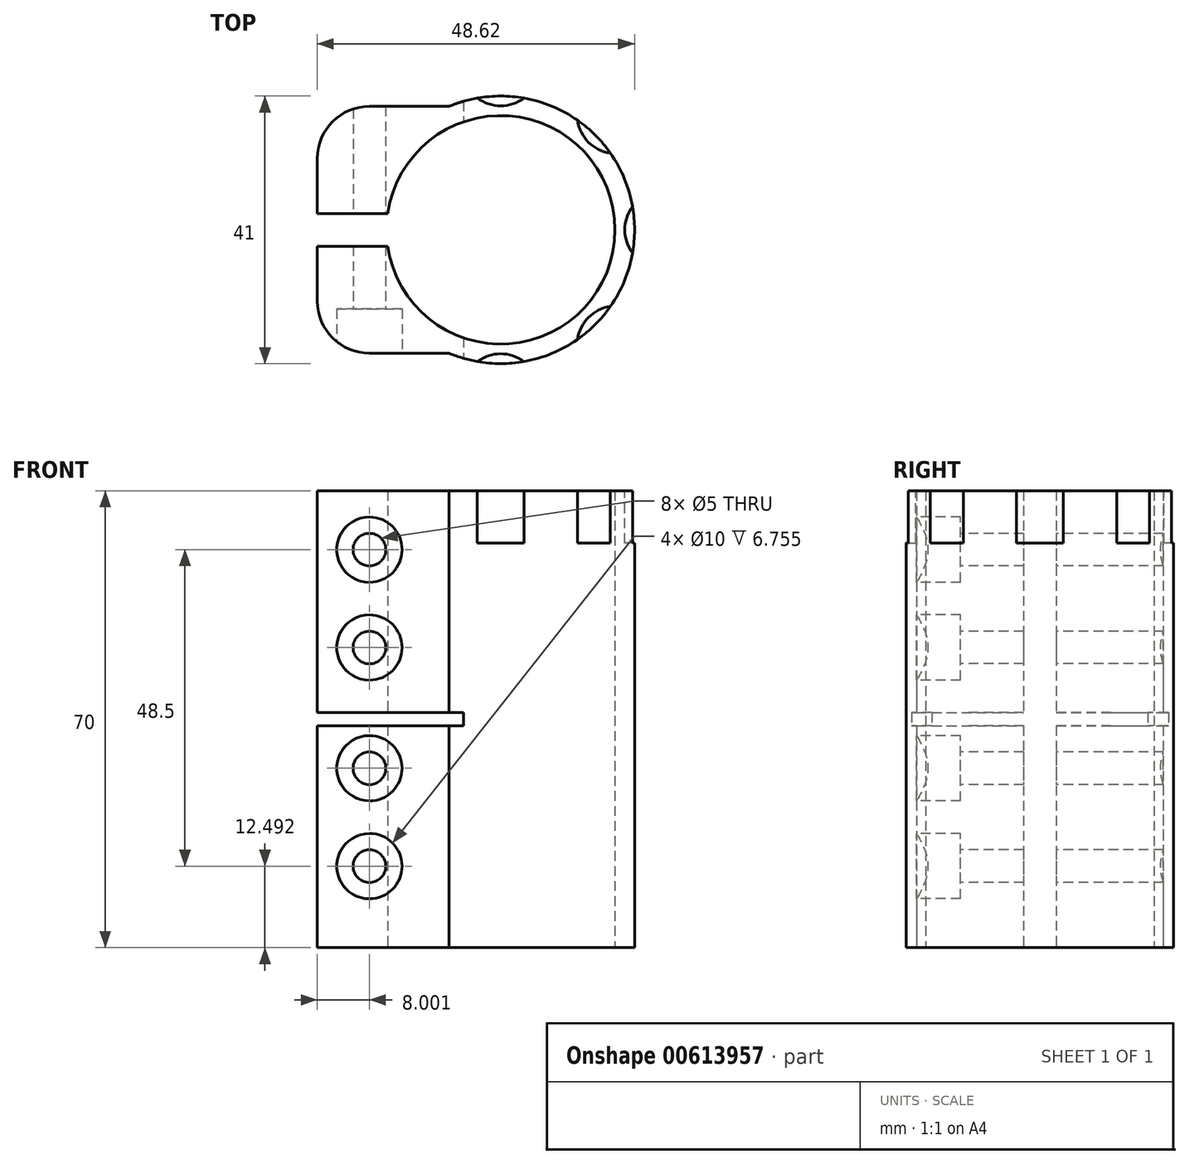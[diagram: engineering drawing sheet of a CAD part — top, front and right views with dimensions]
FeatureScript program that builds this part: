
annotation { "Feature Type Name" : "Feature", "Feature Type Description" : "" }
export const myFeature = defineFeature(function(context is Context, id is Id, definition is map)
    precondition{}
    {
        {
            var Q0;
            Q0=qCreatedBy(makeId("Top.planeOp"),FACE);
            var sketch = newSketch(context, id + "F0", { "sketchPlane" : qUnion([Q0])});
            skArc(sketch, "E0", {"start": v(-17.32, -2.5) * mm, "mid": v(17.5, 0) * mm, "end": v(-17.32, 2.5) * mm});
            skLineSegment(sketch, "E1", {"start": v(-7.92, 18.9) * mm, "end": v(-20.12, 18.9) * mm});
            skLineSegment(sketch, "E2", {"start": v(-28.12, 10.9) * mm, "end": v(-28.12, 2.5) * mm});
            skLineSegment(sketch, "E3", {"start": v(-28.12, 2.5) * mm, "end": v(-17.32, 2.5) * mm});
            skPoint(sketch, "E4.visualSharp", {"position": v(-28.12, 18.9) * mm});
            skArc(sketch, "E4.filletArc", {"start": v(-20.12, 18.9) * mm, "mid": v(-25.78, 16.57) * mm, "end": v(-28.12, 10.9) * mm});
            skLineSegment(sketch, "E5", {"start": v(0, 0) * mm, "end": v(40.9, 0) * mm, "construction": true});
            skArc(sketch, "E6.MirrorCS", {"start": v(-20.12, -18.9) * mm, "mid": v(-25.78, -16.57) * mm, "end": v(-28.12, -10.9) * mm});
            skLineSegment(sketch, "E7.MirrorCS", {"start": v(-7.92, -18.9) * mm, "end": v(-20.12, -18.9) * mm});
            skLineSegment(sketch, "E8.MirrorCS", {"start": v(-28.12, -2.5) * mm, "end": v(-17.32, -2.5) * mm});
            skLineSegment(sketch, "E9.MirrorCS", {"start": v(-28.12, -10.9) * mm, "end": v(-28.12, -2.5) * mm});
            skArc(sketch, "E10.trimOffspring", {"start": v(-7.92, -18.9) * mm, "mid": v(20.5, 0) * mm, "end": v(-7.92, 18.9) * mm});
            skSolve(sketch);
        }
        {
            var Q0;
            Q0 = qSketchRegion(id + "F0", true);
            extrude(context, id + "F1", {"entities" : qUnion([Q0]), "endBound" : BoundingType.SYMMETRIC, "depth" : 70 * mm, "offsetDistance" : 25 * mm});
        }
        {
            var Q0;
            Q0=makeQuery(id+"F1.opExtrude","SWEPT_FACE",FACE,{"disambiguationData":[OSD([sQuery(id+"F0.wireOp",EDGE,"E7.MirrorCS")])]});
            var sketch = newSketch(context, id + "F2", { "sketchPlane" : qUnion([Q0])});
            skPoint(sketch, "E11", {"position": v(-20.12, 26) * mm});
            skPoint(sketch, "E12", {"position": v(-20.12, 11) * mm});
            skPoint(sketch, "E13", {"position": v(-20.12, -7.5) * mm});
            skPoint(sketch, "E14", {"position": v(-20.12, -22.5) * mm});
            skPoint(sketch, "E15", {"position": v(0, 1.74) * mm});
            skSolve(sketch);
        }
        {
            var Q0;
            Q0=sQuery(id+"F2.wireOp",VERTEX,"E14");
            var Q1;
            Q1=sQuery(id+"F2.wireOp",VERTEX,"E13");
            var Q2;
            Q2=sQuery(id+"F2.wireOp",VERTEX,"E11");
            var Q3;
            Q3=sQuery(id+"F2.wireOp",VERTEX,"E12");
            var Q4;
            Q4=makeQuery(id+"F1.opExtrude","SWEPT_BODY",BODY,{"disambiguationData":[OSD([sQuery(id+"F0.wireOp",EDGE,"E0"),sQuery(id+"F0.wireOp",EDGE,"E1"),sQuery(id+"F0.wireOp",EDGE,"E2"),sQuery(id+"F0.wireOp",EDGE,"E3"),sQuery(id+"F0.wireOp",EDGE,"E4.filletArc"),sQuery(id+"F0.wireOp",EDGE,"E6.MirrorCS"),sQuery(id+"F0.wireOp",EDGE,"E7.MirrorCS"),sQuery(id+"F0.wireOp",EDGE,"E8.MirrorCS"),sQuery(id+"F0.wireOp",EDGE,"E9.MirrorCS"),sQuery(id+"F0.wireOp",EDGE,"E10.trimOffspring")])]});
            hole(context, id + "F3", {"style" : HoleStyle.C_BORE, "endStyle" : HoleEndStyle.THROUGH, "holeDiameter" : 5 * mm, "cBoreDiameter" : 10 * mm, "cBoreDepth" : 5 * mm, "majorDiameter" : 5 * mm, "isTappedThrough" : true, "tappedDepth" : 12 * mm, "tapClearance" : 3, "locations" : qUnion([Q0, Q1, Q2, Q3]), "scope" : qUnion([Q4])});
        }
        {
            var Q0;
            Q0=qCreatedBy(makeId("Front.planeOp"),FACE);
            var sketch = newSketch(context, id + "F4", { "sketchPlane" : qUnion([Q0])});
            skLineSegment(sketch, "E16.bottom", {"start": v(-28.12, 1) * mm, "end": v(-5.72, 1) * mm});
            skLineSegment(sketch, "E16.top", {"start": v(-28.12, -1) * mm, "end": v(-5.72, -1) * mm});
            skLineSegment(sketch, "E16.left", {"start": v(-28.12, 1) * mm, "end": v(-28.12, -1) * mm});
            skLineSegment(sketch, "E16.right", {"start": v(-5.72, 1) * mm, "end": v(-5.72, -1) * mm});
            skSolve(sketch);
        }
        {
            var Q0;
            Q0 = qSketchRegion(id + "F4", true);
            extrude(context, id + "F5", {"entities" : qUnion([Q0]), "operationType" : NewBodyOperationType.REMOVE, "endBound" : BoundingType.SYMMETRIC, "oppositeDirection" : true, "depth" : 50 * mm, "offsetDistance" : 25 * mm});
        }
        {
            var Q0;
            Q0=makeQuery(id+"F1.opExtrude","CAP_FACE",FACE,{"disambiguationData":[OSD([sQuery(id+"F0.wireOp",EDGE,"E0"),sQuery(id+"F0.wireOp",EDGE,"E1"),sQuery(id+"F0.wireOp",EDGE,"E2"),sQuery(id+"F0.wireOp",EDGE,"E3"),sQuery(id+"F0.wireOp",EDGE,"E4.filletArc"),sQuery(id+"F0.wireOp",EDGE,"E6.MirrorCS"),sQuery(id+"F0.wireOp",EDGE,"E7.MirrorCS"),sQuery(id+"F0.wireOp",EDGE,"E8.MirrorCS"),sQuery(id+"F0.wireOp",EDGE,"E9.MirrorCS"),sQuery(id+"F0.wireOp",EDGE,"E10.trimOffspring")])],"isStart":false});
            var sketch = newSketch(context, id + "F6", { "sketchPlane" : qUnion([Q0])});
            skCircle(sketch, "E17", {"center": v(0, -25) * mm, "radius": 6 * mm});
            skCircle(sketch, "E18.1.0", {"center": v(17.68, -17.68) * mm, "radius": 6 * mm});
            skCircle(sketch, "E18.2.0", {"center": v(25, 0) * mm, "radius": 6 * mm});
            skCircle(sketch, "E18.3.0", {"center": v(17.68, 17.68) * mm, "radius": 6 * mm});
            skCircle(sketch, "E18.4.0", {"center": v(0, 25) * mm, "radius": 6 * mm});
            skPoint(sketch, "E18.center", {"position": v(0, 0) * mm});
            skLineSegment(sketch, "E18.anchor1", {"start": v(0, 0) * mm, "end": v(0, -25) * mm, "construction": true});
            skLineSegment(sketch, "E18.anchor2", {"start": v(0, 0) * mm, "end": v(0, 25) * mm, "construction": true});
            skSolve(sketch);
        }
        {
            var Q0;
            Q0 = qSketchRegion(id + "F6", true);
            extrude(context, id + "F7", {"entities" : qUnion([Q0]), "operationType" : NewBodyOperationType.REMOVE, "oppositeDirection" : true, "depth" : 8 * mm, "offsetDistance" : 25 * mm});
        }
    });
